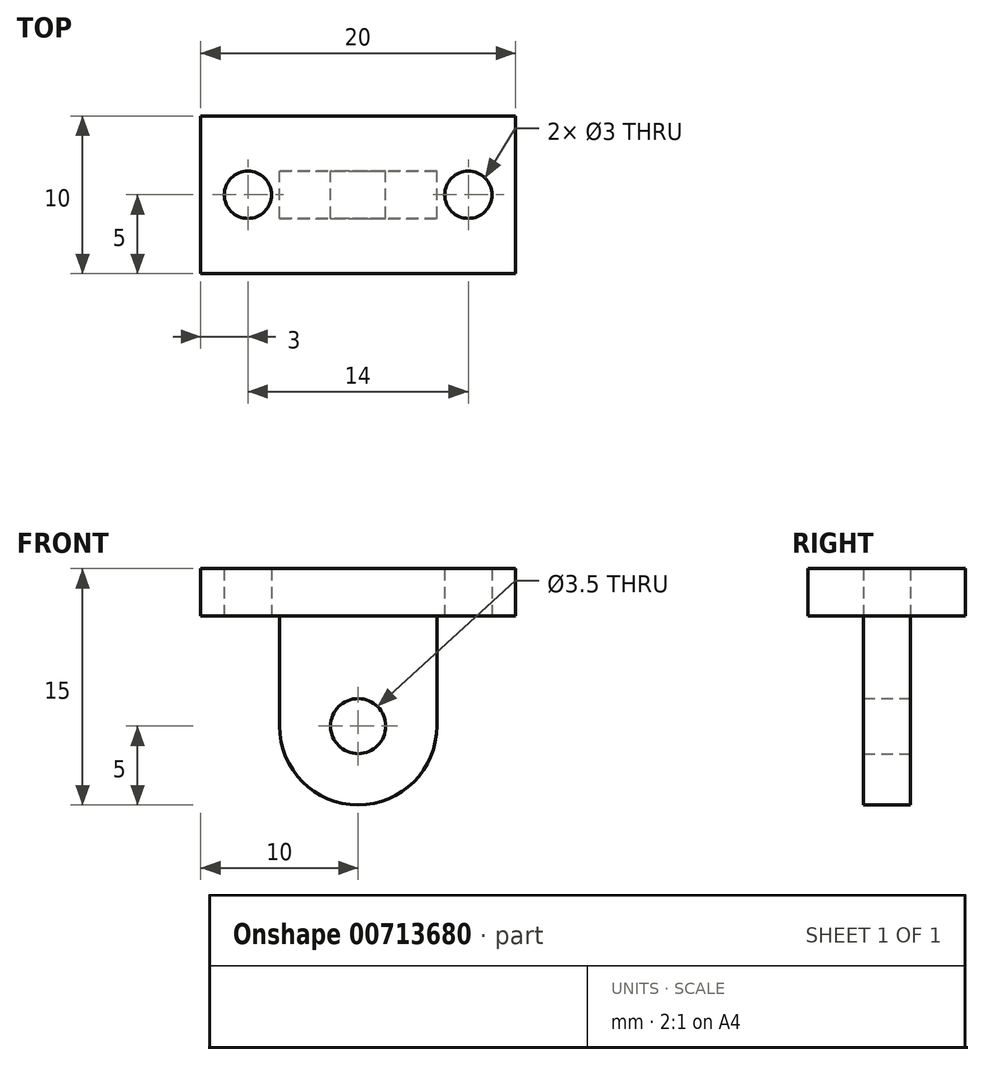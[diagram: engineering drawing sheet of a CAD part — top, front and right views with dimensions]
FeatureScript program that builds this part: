
annotation { "Feature Type Name" : "Feature", "Feature Type Description" : "" }
export const myFeature = defineFeature(function(context is Context, id is Id, definition is map)
    precondition{}
    {
        {
            var Q0;
            Q0=qCreatedBy(makeId("Front.planeOp"),FACE);
            var sketch = newSketch(context, id + "F0", { "sketchPlane" : qUnion([Q0])});
            skLineSegment(sketch, "E0.bottom", {"start": v(10, -1.5) * mm, "end": v(-10, -1.5) * mm});
            skLineSegment(sketch, "E0.top", {"start": v(10, 1.5) * mm, "end": v(-10, 1.5) * mm});
            skLineSegment(sketch, "E0.left", {"start": v(10, -1.5) * mm, "end": v(10, 1.5) * mm});
            skLineSegment(sketch, "E0.right", {"start": v(-10, -1.5) * mm, "end": v(-10, 1.5) * mm});
            skPoint(sketch, "E0.middle", {"position": v(0, 0) * mm});
            skLineSegment(sketch, "E1", {"start": v(0, -1.5) * mm, "end": v(-5, -1.5) * mm});
            skLineSegment(sketch, "E2.bottom", {"start": v(-5, -1.5) * mm, "end": v(5, -1.5) * mm});
            skLineSegment(sketch, "E2.top", {"start": v(-5, -8.5) * mm, "end": v(5, -8.5) * mm});
            skLineSegment(sketch, "E2.left", {"start": v(-5, -1.5) * mm, "end": v(-5, -8.5) * mm});
            skLineSegment(sketch, "E2.right", {"start": v(5, -1.5) * mm, "end": v(5, -8.5) * mm});
            skArc(sketch, "E3", {"start": v(-5, -8.5) * mm, "mid": v(0, -13.5) * mm, "end": v(5, -8.5) * mm});
            skCircle(sketch, "E4", {"center": v(0, -8.5) * mm, "radius": 1.75 * mm});
            skSolve(sketch);
        }
        {
            var Q0;
            Q0=makeQuery(id+"F0.imprint","IMPRINT",FACE,{"disambiguationData":[TD([[makeQuery(id+"F0.imprint","IMPRINT",EDGE,{"derivedFrom":sQuery(id+"F0.wireOp",EDGE,"E0.top")}),1.0]])]});
            extrude(context, id + "F1", {"entities" : qUnion([Q0]), "endBound" : BoundingType.SYMMETRIC, "depth" : 10 * mm, "offsetDistance" : 25 * mm});
        }
        {
            var Q0;
            Q0 = qSketchRegion(id + "F0", true);
            extrude(context, id + "F2", {"entities" : qUnion([Q0]), "operationType" : NewBodyOperationType.ADD, "endBound" : BoundingType.SYMMETRIC, "depth" : 3 * mm, "offsetDistance" : 25 * mm});
        }
        {
            var Q0;
            Q0=makeQuery(id+"F1.opExtrude","SWEPT_FACE",FACE,{"disambiguationData":[OSD([sQuery(id+"F0.wireOp",EDGE,"E0.bottom"),sQuery(id+"F0.wireOp",EDGE,"E2.bottom")])]});
            var sketch = newSketch(context, id + "F3", { "sketchPlane" : qUnion([Q0])});
            skCircle(sketch, "E5", {"center": v(-7, 0) * mm, "radius": 1.5 * mm});
            skCircle(sketch, "E6", {"center": v(7, 0) * mm, "radius": 1.5 * mm});
            skSolve(sketch);
        }
        {
            var Q0;
            Q0=makeQuery(id+"F3.imprint","IMPRINT",FACE,{"disambiguationData":[TD([[makeQuery(id+"F3.imprint","IMPRINT",EDGE,{"derivedFrom":sQuery(id+"F3.wireOp",EDGE,"E5")}),1.0]])]});
            var Q1;
            Q1=makeQuery(id+"F3.imprint","IMPRINT",FACE,{"disambiguationData":[TD([[makeQuery(id+"F3.imprint","IMPRINT",EDGE,{"derivedFrom":sQuery(id+"F3.wireOp",EDGE,"E6")}),1.0]])]});
            extrude(context, id + "F4", {"entities" : qUnion([Q0, Q1]), "operationType" : NewBodyOperationType.REMOVE, "endBound" : BoundingType.THROUGH_ALL, "oppositeDirection" : true, "depth" : 3 * mm, "offsetDistance" : 25 * mm});
        }
    });
